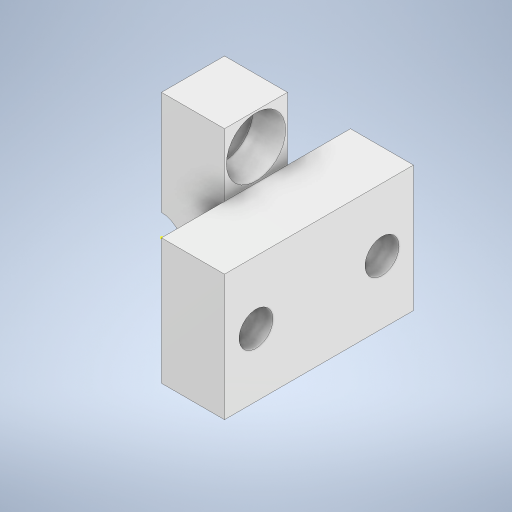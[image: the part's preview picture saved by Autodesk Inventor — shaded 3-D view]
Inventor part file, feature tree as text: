
AUTODESK INVENTOR PART (.ipt)
format: ipt  version: 2023 (Build 270158000, 158)  size: 342,016 bytes
history: native  units: mm
features: sketch x10, extrude x9, plane x1
ambient origin geometry x8: Origin, YZ Plane, XZ Plane, XY Plane, X Axis, Y Axis, Z Axis, Center Point
bodies: Solid1 (feature_tree)
feature tree (20):
  extrude  "Extrusion1"  Depth=20.0mm
  plane  "Work Plane1"
  extrude  "Extrusion2"  Depth=5.0mm
  extrude  "Extrusion3"  Depth=3.5mm
  extrude  "Extrusion4"  Depth=2.5mm
  extrude  "Extrusion5"  Depth=2.5mm
  sketch  "Sketch6"  dims[d21=2.5mm d22=2.7mm]
  extrude  "Extrusion6"  Depth=2.5mm
  extrude  "Extrusion7"  Depth=25.0mm TaperAngle=0.0deg
  extrude  "Extrusion8"  Depth=4.0mm
  extrude  "Extrusion9"  Depth=5.0mm
  sketch  "Sketch1"  dims[d0=20.0mm d1=20.0mm]
  sketch  "Sketch2"  dims[d10=5.0mm d11=0.0mm d12=5.0mm]
  sketch  "Sketch3"  dims[d13=2.0mm d14=0.0mm d15=3.5mm]
  sketch  "Sketch4"  dims[d16=8.0mm d17=0.0mm d18=2.5mm]
  sketch  "Sketch5"  dims[d19=2.5mm d20=2.5mm]
  sketch  "Sketch7"  dims[d23=2.7mm d24=25.0mm d25=0.0mm]
  sketch  "Sketch8"  dims[d26=4.0mm d27=4.0mm]
  sketch  "Sketch9"  dims[d28=4.0mm d29=0.0mm d30=5.0mm]
  sketch  "Sketch10"  dims[d31=5.0mm d32=5.0mm d33=5.0mm d34=10.0mm d35=0.0mm d36=5.0mm d37=5.0mm d38=5.0mm d39=2.7mm d40=2.7mm d41=5.0mm d42=5.0mm d43=5.0mm d44=5.0mm d45=2.5mm d46=2.5mm d47=5.0mm d48=0.0mm d49=4.0mm d50=4.0mm d51=2.0mm d52=0.0mm d53=4.7mm d54=4.7mm d55=2.6mm d56=0.0mm]
